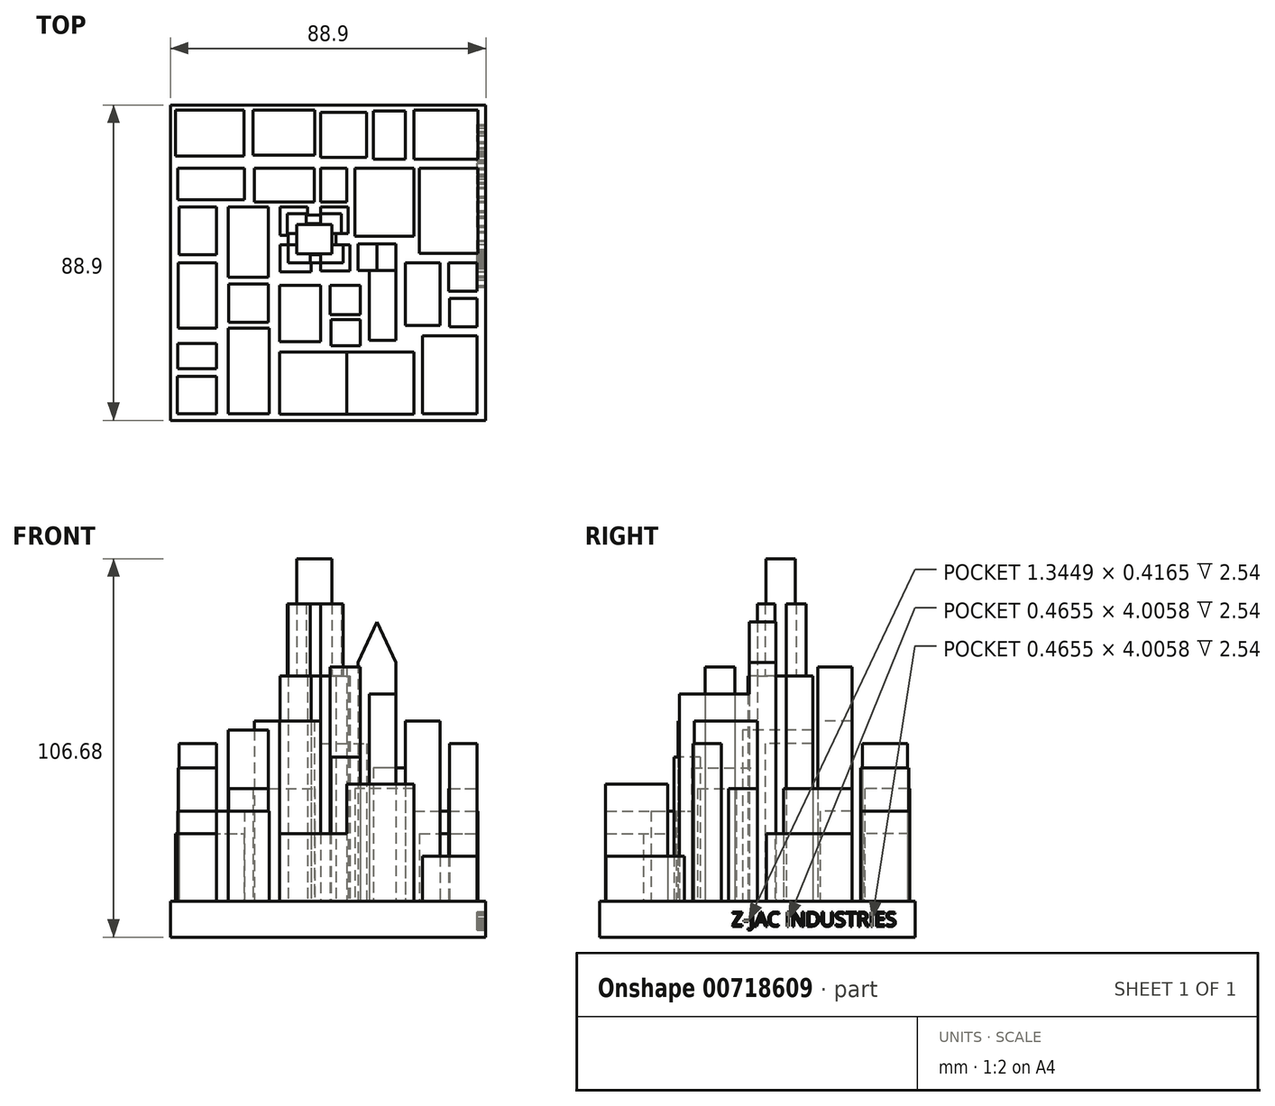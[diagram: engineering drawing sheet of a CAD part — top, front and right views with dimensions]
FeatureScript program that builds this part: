
annotation { "Feature Type Name" : "Feature", "Feature Type Description" : "" }
export const myFeature = defineFeature(function(context is Context, id is Id, definition is map)
    precondition{}
    {
        {
            var Q0;
            Q0=qCreatedBy(makeId("Top.planeOp"),FACE);
            var sketch = newSketch(context, id + "F0", { "sketchPlane" : qUnion([Q0])});
            skLineSegment(sketch, "E0", {"start": v(0, 0) * mm, "end": v(0, 44.45) * mm});
            skLineSegment(sketch, "E1", {"start": v(0, 44.45) * mm, "end": v(46.53, 44.45) * mm});
            skLineSegment(sketch, "E2", {"start": v(46.53, 44.45) * mm, "end": v(46.53, -44.45) * mm});
            skLineSegment(sketch, "E3", {"start": v(46.53, -44.45) * mm, "end": v(-42.37, -44.45) * mm});
            skLineSegment(sketch, "E4", {"start": v(-42.37, -44.45) * mm, "end": v(-42.37, 44.45) * mm});
            skLineSegment(sketch, "E5", {"start": v(-42.37, 44.45) * mm, "end": v(0, 44.45) * mm});
            skSolve(sketch);
        }
        {
            var Q0;
            Q0 = qSketchRegion(id + "F0", true);
            var Q1;
            Q1=makeQuery(id+"F0.imprint","IMPRINT",FACE,{"disambiguationData":[TD([[makeQuery(id+"F0.imprint","IMPRINT",EDGE,{"derivedFrom":sQuery(id+"F0.wireOp",EDGE,"E1")}),-1.0]])]});
            extrude(context, id + "F1", {"entities" : qUnion([Q0, Q1]), "depth" : 10.16 * mm, "offsetDistance" : 25.4 * mm});
        }
        {
            var Q0;
            Q0=makeQuery(id+"F1.opExtrude","CAP_FACE",FACE,{"disambiguationData":[OSD([sQuery(id+"F0.wireOp",EDGE,"E1"),sQuery(id+"F0.wireOp",EDGE,"E2"),sQuery(id+"F0.wireOp",EDGE,"E3"),sQuery(id+"F0.wireOp",EDGE,"E4"),sQuery(id+"F0.wireOp",EDGE,"E5")])],"isStart":false});
            var sketch = newSketch(context, id + "F2", { "sketchPlane" : qUnion([Q0])});
            skLineSegment(sketch, "E6.bottom", {"start": v(-40.9, 43.05) * mm, "end": v(-21.56, 43.05) * mm});
            skLineSegment(sketch, "E6.top", {"start": v(-40.9, 29.98) * mm, "end": v(-21.56, 29.98) * mm});
            skLineSegment(sketch, "E6.left", {"start": v(-40.9, 43.05) * mm, "end": v(-40.9, 29.98) * mm});
            skLineSegment(sketch, "E6.right", {"start": v(-21.56, 43.05) * mm, "end": v(-21.56, 29.98) * mm});
            skLineSegment(sketch, "E7.bottom", {"start": v(-11.52, -42.72) * mm, "end": v(26.25, -42.72) * mm});
            skLineSegment(sketch, "E7.top", {"start": v(-11.52, -25.17) * mm, "end": v(26.25, -25.17) * mm});
            skLineSegment(sketch, "E7.left", {"start": v(-11.52, -42.72) * mm, "end": v(-11.52, -25.17) * mm});
            skLineSegment(sketch, "E7.right", {"start": v(26.25, -42.72) * mm, "end": v(26.25, -25.17) * mm});
            skLineSegment(sketch, "E8.bottom", {"start": v(27.79, 26.67) * mm, "end": v(44.29, 26.67) * mm});
            skLineSegment(sketch, "E8.top", {"start": v(27.79, 2.59) * mm, "end": v(44.29, 2.59) * mm});
            skLineSegment(sketch, "E8.left", {"start": v(27.79, 26.67) * mm, "end": v(27.79, 2.59) * mm});
            skLineSegment(sketch, "E8.right", {"start": v(44.29, 26.67) * mm, "end": v(44.29, 2.59) * mm});
            skLineSegment(sketch, "E9.bottom", {"start": v(-40.37, -42.59) * mm, "end": v(-29.36, -42.59) * mm});
            skLineSegment(sketch, "E9.top", {"start": v(-40.37, -32.12) * mm, "end": v(-29.36, -32.12) * mm});
            skLineSegment(sketch, "E9.left", {"start": v(-40.37, -42.59) * mm, "end": v(-40.37, -32.12) * mm});
            skLineSegment(sketch, "E9.right", {"start": v(-29.36, -42.59) * mm, "end": v(-29.36, -32.12) * mm});
            skSolve(sketch);
        }
        {
            var Q0;
            Q0 = qSketchRegion(id + "F2", true);
            extrude(context, id + "F3", {"entities" : qUnion([Q0]), "operationType" : NewBodyOperationType.ADD, "depth" : 19.05 * mm, "offsetDistance" : 25.4 * mm});
        }
        {
            var Q0;
            Q0=makeQuery(id+"F1.opExtrude","CAP_FACE",FACE,{"disambiguationData":[OSD([sQuery(id+"F0.wireOp",EDGE,"E1"),sQuery(id+"F0.wireOp",EDGE,"E2"),sQuery(id+"F0.wireOp",EDGE,"E3"),sQuery(id+"F0.wireOp",EDGE,"E4"),sQuery(id+"F0.wireOp",EDGE,"E5")])],"isStart":false});
            var sketch = newSketch(context, id + "F4", { "sketchPlane" : qUnion([Q0])});
            skLineSegment(sketch, "E10.bottom", {"start": v(-26.07, -42.59) * mm, "end": v(-14.5, -42.59) * mm});
            skLineSegment(sketch, "E10.top", {"start": v(-26.07, -18.49) * mm, "end": v(-14.5, -18.49) * mm});
            skLineSegment(sketch, "E10.left", {"start": v(-26.07, -42.59) * mm, "end": v(-26.07, -18.49) * mm});
            skLineSegment(sketch, "E10.right", {"start": v(-14.5, -42.59) * mm, "end": v(-14.5, -18.49) * mm});
            skLineSegment(sketch, "E11.bottom", {"start": v(-29.36, -29.86) * mm, "end": v(-40.29, -29.86) * mm});
            skLineSegment(sketch, "E11.top", {"start": v(-29.36, -22.85) * mm, "end": v(-40.29, -22.85) * mm});
            skLineSegment(sketch, "E11.left", {"start": v(-29.36, -29.86) * mm, "end": v(-29.36, -22.85) * mm});
            skLineSegment(sketch, "E11.right", {"start": v(-40.29, -29.86) * mm, "end": v(-40.29, -22.85) * mm});
            skLineSegment(sketch, "E12.bottom", {"start": v(26.26, 42.94) * mm, "end": v(44.27, 42.94) * mm});
            skLineSegment(sketch, "E12.top", {"start": v(26.26, 29.1) * mm, "end": v(44.27, 29.1) * mm});
            skLineSegment(sketch, "E12.left", {"start": v(26.26, 42.94) * mm, "end": v(26.26, 29.1) * mm});
            skLineSegment(sketch, "E12.right", {"start": v(44.27, 42.94) * mm, "end": v(44.27, 29.1) * mm});
            skLineSegment(sketch, "E13.bottom", {"start": v(-40.29, 26.67) * mm, "end": v(-21.52, 26.67) * mm});
            skLineSegment(sketch, "E13.top", {"start": v(-40.29, 17.73) * mm, "end": v(-21.52, 17.73) * mm});
            skLineSegment(sketch, "E13.left", {"start": v(-40.29, 26.67) * mm, "end": v(-40.29, 17.73) * mm});
            skLineSegment(sketch, "E13.right", {"start": v(-21.52, 26.67) * mm, "end": v(-21.52, 17.73) * mm});
            skSolve(sketch);
        }
        {
            var Q0;
            Q0 = qSketchRegion(id + "F4", true);
            extrude(context, id + "F5", {"entities" : qUnion([Q0]), "operationType" : NewBodyOperationType.ADD, "depth" : 25.4 * mm, "offsetDistance" : 25.4 * mm});
        }
        {
            var Q0;
            Q0=makeQuery(id+"F1.opExtrude","CAP_FACE",FACE,{"disambiguationData":[OSD([sQuery(id+"F0.wireOp",EDGE,"E1"),sQuery(id+"F0.wireOp",EDGE,"E2"),sQuery(id+"F0.wireOp",EDGE,"E3"),sQuery(id+"F0.wireOp",EDGE,"E4"),sQuery(id+"F0.wireOp",EDGE,"E5")])],"isStart":false});
            var sketch = newSketch(context, id + "F6", { "sketchPlane" : qUnion([Q0])});
            skLineSegment(sketch, "E14.bottom", {"start": v(-14.7, -16.78) * mm, "end": v(-25.88, -16.78) * mm});
            skLineSegment(sketch, "E14.top", {"start": v(-14.7, -5.97) * mm, "end": v(-25.88, -5.97) * mm});
            skLineSegment(sketch, "E14.left", {"start": v(-14.7, -16.78) * mm, "end": v(-14.7, -5.97) * mm});
            skLineSegment(sketch, "E14.right", {"start": v(-25.88, -16.78) * mm, "end": v(-25.88, -5.97) * mm});
            skLineSegment(sketch, "E15.bottom", {"start": v(-19.05, 42.94) * mm, "end": v(-1.61, 42.94) * mm});
            skLineSegment(sketch, "E15.top", {"start": v(-19.05, 30.24) * mm, "end": v(-1.61, 30.24) * mm});
            skLineSegment(sketch, "E15.left", {"start": v(-19.05, 42.94) * mm, "end": v(-19.05, 30.24) * mm});
            skLineSegment(sketch, "E15.right", {"start": v(-1.61, 42.94) * mm, "end": v(-1.61, 30.24) * mm});
            skPoint(sketch, "E16.firstSnap0", {"position": v(36.04, 2.59) * mm});
            skLineSegment(sketch, "E16.bottom", {"start": v(36.04, 0) * mm, "end": v(44.08, 0) * mm});
            skLineSegment(sketch, "E16.top", {"start": v(36.04, -8.06) * mm, "end": v(44.08, -8.06) * mm});
            skLineSegment(sketch, "E16.left", {"start": v(36.04, 0) * mm, "end": v(36.04, -8.06) * mm});
            skLineSegment(sketch, "E16.right", {"start": v(44.08, 0) * mm, "end": v(44.08, -8.06) * mm});
            skPoint(sketch, "E17.firstSnap0", {"position": v(-30.9, 26.67) * mm});
            skPoint(sketch, "E17.firstSnap1", {"position": v(26.25, -33.95) * mm});
            skLineSegment(sketch, "E17.bottom", {"start": v(26.25, 26.67) * mm, "end": v(9.57, 26.67) * mm});
            skLineSegment(sketch, "E17.top", {"start": v(26.25, 7.49) * mm, "end": v(9.57, 7.49) * mm});
            skLineSegment(sketch, "E17.left", {"start": v(26.25, 26.67) * mm, "end": v(26.25, 7.49) * mm});
            skLineSegment(sketch, "E17.right", {"start": v(9.57, 26.67) * mm, "end": v(9.57, 7.49) * mm});
            skSolve(sketch);
        }
        {
            var Q0;
            Q0 = qSketchRegion(id + "F6", true);
            extrude(context, id + "F7", {"entities" : qUnion([Q0]), "operationType" : NewBodyOperationType.ADD, "depth" : 31.75 * mm, "offsetDistance" : 25.4 * mm});
        }
        {
            var Q0;
            Q0=makeQuery(id+"F1.opExtrude","CAP_FACE",FACE,{"disambiguationData":[OSD([sQuery(id+"F0.wireOp",EDGE,"E1"),sQuery(id+"F0.wireOp",EDGE,"E2"),sQuery(id+"F0.wireOp",EDGE,"E3"),sQuery(id+"F0.wireOp",EDGE,"E4"),sQuery(id+"F0.wireOp",EDGE,"E5")])],"isStart":false});
            var sketch = newSketch(context, id + "F8", { "sketchPlane" : qUnion([Q0])});
            skLineSegment(sketch, "E18.bottom", {"start": v(23.8, 29.1) * mm, "end": v(14.88, 29.1) * mm});
            skLineSegment(sketch, "E18.top", {"start": v(23.8, 42.75) * mm, "end": v(14.88, 42.75) * mm});
            skLineSegment(sketch, "E18.left", {"start": v(23.8, 29.1) * mm, "end": v(23.8, 42.75) * mm});
            skLineSegment(sketch, "E18.right", {"start": v(14.88, 29.1) * mm, "end": v(14.88, 42.75) * mm});
            skLineSegment(sketch, "E19.bottom", {"start": v(-29.36, -18.49) * mm, "end": v(-40.1, -18.49) * mm});
            skLineSegment(sketch, "E19.top", {"start": v(-29.36, 0) * mm, "end": v(-40.1, 0) * mm});
            skLineSegment(sketch, "E19.left", {"start": v(-29.36, -18.49) * mm, "end": v(-29.36, 0) * mm});
            skLineSegment(sketch, "E19.right", {"start": v(-40.1, -18.49) * mm, "end": v(-40.1, 0) * mm});
            skSolve(sketch);
        }
        {
            var Q0;
            Q0 = qSketchRegion(id + "F8", true);
            extrude(context, id + "F9", {"entities" : qUnion([Q0]), "operationType" : NewBodyOperationType.ADD, "depth" : 37.6 * mm, "offsetDistance" : 25.4 * mm});
        }
        {
            var Q0;
            Q0=makeQuery(id+"F1.opExtrude","CAP_FACE",FACE,{"disambiguationData":[OSD([sQuery(id+"F0.wireOp",EDGE,"E1"),sQuery(id+"F0.wireOp",EDGE,"E2"),sQuery(id+"F0.wireOp",EDGE,"E3"),sQuery(id+"F0.wireOp",EDGE,"E4"),sQuery(id+"F0.wireOp",EDGE,"E5")])],"isStart":false});
            var sketch = newSketch(context, id + "F10", { "sketchPlane" : qUnion([Q0])});
            skLineSegment(sketch, "E20.bottom", {"start": v(-39.91, 15.64) * mm, "end": v(-29.36, 15.64) * mm});
            skLineSegment(sketch, "E20.top", {"start": v(-39.91, 2.18) * mm, "end": v(-29.36, 2.18) * mm});
            skLineSegment(sketch, "E20.left", {"start": v(-39.91, 15.64) * mm, "end": v(-39.91, 2.18) * mm});
            skLineSegment(sketch, "E20.right", {"start": v(-29.36, 15.64) * mm, "end": v(-29.36, 2.18) * mm});
            skLineSegment(sketch, "E21.bottom", {"start": v(36.3, -10.14) * mm, "end": v(44.08, -10.14) * mm});
            skLineSegment(sketch, "E21.top", {"start": v(36.3, -18.1) * mm, "end": v(44.08, -18.1) * mm});
            skLineSegment(sketch, "E21.left", {"start": v(36.3, -10.14) * mm, "end": v(36.3, -18.1) * mm});
            skLineSegment(sketch, "E21.right", {"start": v(44.08, -10.14) * mm, "end": v(44.08, -18.1) * mm});
            skLineSegment(sketch, "E22.bottom", {"start": v(0, 42.37) * mm, "end": v(12.99, 42.37) * mm});
            skLineSegment(sketch, "E22.top", {"start": v(0, 29.67) * mm, "end": v(12.99, 29.67) * mm});
            skLineSegment(sketch, "E22.left", {"start": v(0, 42.37) * mm, "end": v(0, 29.67) * mm});
            skLineSegment(sketch, "E22.right", {"start": v(12.99, 42.37) * mm, "end": v(12.99, 29.67) * mm});
            skSolve(sketch);
        }
        {
            var Q0;
            Q0 = qSketchRegion(id + "F10", true);
            extrude(context, id + "F11", {"entities" : qUnion([Q0]), "operationType" : NewBodyOperationType.ADD, "depth" : 44.45 * mm, "offsetDistance" : 25.4 * mm});
        }
        {
            var Q0;
            Q0=makeQuery(id+"F1.opExtrude","CAP_FACE",FACE,{"disambiguationData":[OSD([sQuery(id+"F0.wireOp",EDGE,"E1"),sQuery(id+"F0.wireOp",EDGE,"E2"),sQuery(id+"F0.wireOp",EDGE,"E3"),sQuery(id+"F0.wireOp",EDGE,"E4"),sQuery(id+"F0.wireOp",EDGE,"E5")])],"isStart":false});
            var sketch = newSketch(context, id + "F12", { "sketchPlane" : qUnion([Q0])});
            skLineSegment(sketch, "E23.bottom", {"start": v(-26.07, 15.64) * mm, "end": v(-14.7, 15.64) * mm});
            skLineSegment(sketch, "E23.top", {"start": v(-26.07, -4.08) * mm, "end": v(-14.7, -4.08) * mm});
            skLineSegment(sketch, "E23.left", {"start": v(-26.07, 15.64) * mm, "end": v(-26.07, -4.08) * mm});
            skLineSegment(sketch, "E23.right", {"start": v(-14.7, 15.64) * mm, "end": v(-14.7, -4.08) * mm});
            skSolve(sketch);
        }
        {
            var Q0;
            Q0 = qSketchRegion(id + "F12", true);
            extrude(context, id + "F13", {"entities" : qUnion([Q0]), "operationType" : NewBodyOperationType.ADD, "depth" : 48.26 * mm, "offsetDistance" : 25.4 * mm});
        }
        {
            var Q0;
            Q0=makeQuery(id+"F1.opExtrude","CAP_FACE",FACE,{"disambiguationData":[OSD([sQuery(id+"F0.wireOp",EDGE,"E1"),sQuery(id+"F0.wireOp",EDGE,"E2"),sQuery(id+"F0.wireOp",EDGE,"E3"),sQuery(id+"F0.wireOp",EDGE,"E4"),sQuery(id+"F0.wireOp",EDGE,"E5")])],"isStart":false});
            var sketch = newSketch(context, id + "F14", { "sketchPlane" : qUnion([Q0])});
            skLineSegment(sketch, "E24.bottom", {"start": v(44.08, -20.57) * mm, "end": v(28.72, -20.57) * mm});
            skLineSegment(sketch, "E24.top", {"start": v(44.08, -42.56) * mm, "end": v(28.72, -42.56) * mm});
            skLineSegment(sketch, "E24.left", {"start": v(44.08, -20.57) * mm, "end": v(44.08, -42.56) * mm});
            skLineSegment(sketch, "E24.right", {"start": v(28.72, -20.57) * mm, "end": v(28.72, -42.56) * mm});
            skSolve(sketch);
        }
        {
            var Q0;
            Q0 = qSketchRegion(id + "F14", true);
            extrude(context, id + "F15", {"entities" : qUnion([Q0]), "operationType" : NewBodyOperationType.ADD, "depth" : 12.7 * mm, "offsetDistance" : 25.4 * mm});
        }
        {
            var Q0;
            Q0=makeQuery(id+"F1.opExtrude","CAP_FACE",FACE,{"disambiguationData":[OSD([sQuery(id+"F0.wireOp",EDGE,"E1"),sQuery(id+"F0.wireOp",EDGE,"E2"),sQuery(id+"F0.wireOp",EDGE,"E3"),sQuery(id+"F0.wireOp",EDGE,"E4"),sQuery(id+"F0.wireOp",EDGE,"E5")])],"isStart":false});
            var sketch = newSketch(context, id + "F16", { "sketchPlane" : qUnion([Q0])});
            skPoint(sketch, "E25.oppositeSnap0", {"position": v(9.57, 17.08) * mm});
            skLineSegment(sketch, "E25.bottom", {"start": v(-18.68, 26.67) * mm, "end": v(-1.8, 26.67) * mm});
            skLineSegment(sketch, "E25.top", {"start": v(-18.68, 17.08) * mm, "end": v(-1.8, 17.08) * mm});
            skLineSegment(sketch, "E25.left", {"start": v(-18.68, 26.67) * mm, "end": v(-18.68, 17.08) * mm});
            skLineSegment(sketch, "E25.right", {"start": v(-1.8, 26.67) * mm, "end": v(-1.8, 17.08) * mm});
            skLineSegment(sketch, "E26.bottom", {"start": v(33.65, 0) * mm, "end": v(23.8, 0) * mm});
            skLineSegment(sketch, "E26.top", {"start": v(33.65, -17.73) * mm, "end": v(23.8, -17.73) * mm});
            skLineSegment(sketch, "E26.left", {"start": v(33.65, 0) * mm, "end": v(33.65, -17.73) * mm});
            skLineSegment(sketch, "E26.right", {"start": v(23.8, 0) * mm, "end": v(23.8, -17.73) * mm});
            skLineSegment(sketch, "E27.bottom", {"start": v(-11.52, -22.28) * mm, "end": v(0, -22.28) * mm});
            skLineSegment(sketch, "E27.top", {"start": v(-11.52, -6.35) * mm, "end": v(0, -6.35) * mm});
            skLineSegment(sketch, "E27.left", {"start": v(-11.52, -22.28) * mm, "end": v(-11.52, -6.35) * mm});
            skLineSegment(sketch, "E27.right", {"start": v(0, -22.28) * mm, "end": v(0, -6.35) * mm});
            skSolve(sketch);
        }
        {
            var Q0;
            Q0 = qSketchRegion(id + "F16", true);
            extrude(context, id + "F17", {"entities" : qUnion([Q0]), "operationType" : NewBodyOperationType.ADD, "depth" : 50.8 * mm, "offsetDistance" : 25.4 * mm});
        }
        {
            var Q0;
            Q0=makeQuery(id+"F1.opExtrude","CAP_FACE",FACE,{"disambiguationData":[OSD([sQuery(id+"F0.wireOp",EDGE,"E1"),sQuery(id+"F0.wireOp",EDGE,"E2"),sQuery(id+"F0.wireOp",EDGE,"E3"),sQuery(id+"F0.wireOp",EDGE,"E4"),sQuery(id+"F0.wireOp",EDGE,"E5")])],"isStart":false});
            var sketch = newSketch(context, id + "F18", { "sketchPlane" : qUnion([Q0])});
            skLineSegment(sketch, "E28.bottom", {"start": v(-9.2, 13.46) * mm, "end": v(4.27, 13.46) * mm});
            skLineSegment(sketch, "E28.top", {"start": v(-9.2, 0) * mm, "end": v(4.27, 0) * mm});
            skLineSegment(sketch, "E28.left", {"start": v(-9.2, 13.46) * mm, "end": v(-9.2, 0) * mm});
            skLineSegment(sketch, "E28.right", {"start": v(4.27, 13.46) * mm, "end": v(4.27, 0) * mm});
            skLineSegment(sketch, "E29.bottom", {"start": v(-11.47, 15.64) * mm, "end": v(-3.7, 15.64) * mm});
            skLineSegment(sketch, "E29.top", {"start": v(-11.47, 7.68) * mm, "end": v(-3.7, 7.68) * mm});
            skLineSegment(sketch, "E29.left", {"start": v(-11.47, 15.64) * mm, "end": v(-11.47, 7.68) * mm});
            skLineSegment(sketch, "E29.right", {"start": v(-3.7, 15.64) * mm, "end": v(-3.7, 7.68) * mm});
            skLineSegment(sketch, "E30.bottom", {"start": v(0, 15.64) * mm, "end": v(7.68, 15.64) * mm});
            skLineSegment(sketch, "E30.top", {"start": v(0, 8.25) * mm, "end": v(7.68, 8.25) * mm});
            skLineSegment(sketch, "E30.left", {"start": v(0, 15.64) * mm, "end": v(0, 8.25) * mm});
            skLineSegment(sketch, "E30.right", {"start": v(7.68, 15.64) * mm, "end": v(7.68, 8.25) * mm});
            skLineSegment(sketch, "E31.bottom", {"start": v(0, 5.02) * mm, "end": v(8.25, 5.02) * mm});
            skLineSegment(sketch, "E31.top", {"start": v(0, -2.37) * mm, "end": v(8.25, -2.37) * mm});
            skLineSegment(sketch, "E31.left", {"start": v(0, 5.02) * mm, "end": v(0, -2.37) * mm});
            skLineSegment(sketch, "E31.right", {"start": v(8.25, 5.02) * mm, "end": v(8.25, -2.37) * mm});
            skLineSegment(sketch, "E32.bottom", {"start": v(-2.75, 5.02) * mm, "end": v(-11.47, 5.02) * mm});
            skLineSegment(sketch, "E32.top", {"start": v(-2.75, -2.56) * mm, "end": v(-11.47, -2.56) * mm});
            skLineSegment(sketch, "E32.left", {"start": v(-2.75, 5.02) * mm, "end": v(-2.75, -2.56) * mm});
            skLineSegment(sketch, "E32.right", {"start": v(-11.47, 5.02) * mm, "end": v(-11.47, -2.56) * mm});
            skSolve(sketch);
        }
        {
            var Q0;
            Q0 = qSketchRegion(id + "F18", true);
            extrude(context, id + "F19", {"entities" : qUnion([Q0]), "operationType" : NewBodyOperationType.ADD, "depth" : 63.5 * mm, "offsetDistance" : 25.4 * mm});
        }
        {
            var Q0;
            Q0=makeQuery(id+"F19.opExtrude","CAP_FACE",FACE,{"disambiguationData":[OSD([sQuery(id+"F18.wireOp",EDGE,"E28.bottom"),sQuery(id+"F18.wireOp",EDGE,"E28.top"),sQuery(id+"F18.wireOp",EDGE,"E28.left"),sQuery(id+"F18.wireOp",EDGE,"E28.right"),sQuery(id+"F18.wireOp",EDGE,"E29.bottom"),sQuery(id+"F18.wireOp",EDGE,"E29.top"),sQuery(id+"F18.wireOp",EDGE,"E29.left"),sQuery(id+"F18.wireOp",EDGE,"E29.right"),sQuery(id+"F18.wireOp",EDGE,"E30.bottom"),sQuery(id+"F18.wireOp",EDGE,"E30.top"),sQuery(id+"F18.wireOp",EDGE,"E30.left"),sQuery(id+"F18.wireOp",EDGE,"E30.right"),sQuery(id+"F18.wireOp",EDGE,"E31.bottom"),sQuery(id+"F18.wireOp",EDGE,"E31.top"),sQuery(id+"F18.wireOp",EDGE,"E31.left"),sQuery(id+"F18.wireOp",EDGE,"E31.right"),sQuery(id+"F18.wireOp",EDGE,"E32.bottom"),sQuery(id+"F18.wireOp",EDGE,"E32.top"),sQuery(id+"F18.wireOp",EDGE,"E32.left"),sQuery(id+"F18.wireOp",EDGE,"E32.right")])],"isStart":false});
            var sketch = newSketch(context, id + "F20", { "sketchPlane" : qUnion([Q0])});
            skLineSegment(sketch, "E33.bottom", {"start": v(-9.39, 13.75) * mm, "end": v(-4.08, 13.75) * mm});
            skLineSegment(sketch, "E33.top", {"start": v(-9.39, 8.25) * mm, "end": v(-4.08, 8.25) * mm});
            skLineSegment(sketch, "E33.left", {"start": v(-9.39, 13.75) * mm, "end": v(-9.39, 8.25) * mm});
            skLineSegment(sketch, "E33.right", {"start": v(-4.08, 13.75) * mm, "end": v(-4.08, 8.25) * mm});
            skLineSegment(sketch, "E34.bottom", {"start": v(-9.2, 0) * mm, "end": v(-2.94, 0) * mm});
            skLineSegment(sketch, "E34.top", {"start": v(-9.2, 5.02) * mm, "end": v(-2.94, 5.02) * mm});
            skLineSegment(sketch, "E34.left", {"start": v(-9.2, 0) * mm, "end": v(-9.2, 5.02) * mm});
            skLineSegment(sketch, "E34.right", {"start": v(-2.94, 0) * mm, "end": v(-2.94, 5.02) * mm});
            skLineSegment(sketch, "E35.bottom", {"start": v(6.35, 0) * mm, "end": v(0, 0) * mm});
            skLineSegment(sketch, "E35.top", {"start": v(6.35, 5.02) * mm, "end": v(0, 5.02) * mm});
            skLineSegment(sketch, "E35.left", {"start": v(6.35, 0) * mm, "end": v(6.35, 5.02) * mm});
            skLineSegment(sketch, "E35.right", {"start": v(0, 0) * mm, "end": v(0, 5.02) * mm});
            skLineSegment(sketch, "E36.bottom", {"start": v(5.78, 13.75) * mm, "end": v(0, 13.75) * mm});
            skLineSegment(sketch, "E36.top", {"start": v(5.78, 8.25) * mm, "end": v(0, 8.25) * mm});
            skLineSegment(sketch, "E36.left", {"start": v(5.78, 13.75) * mm, "end": v(5.78, 8.25) * mm});
            skLineSegment(sketch, "E36.right", {"start": v(0, 13.75) * mm, "end": v(0, 8.25) * mm});
            skPoint(sketch, "E37.firstSnap0", {"position": v(-6.73, 13.75) * mm});
            skPoint(sketch, "E37.firstSnap1", {"position": v(-4.08, 11) * mm});
            skPoint(sketch, "E37.oppositeSnap0", {"position": v(3.18, 5.02) * mm});
            skLineSegment(sketch, "E37.bottom", {"start": v(-6.73, 11) * mm, "end": v(3.18, 11) * mm});
            skLineSegment(sketch, "E37.top", {"start": v(-6.73, 2.18) * mm, "end": v(3.18, 2.18) * mm});
            skLineSegment(sketch, "E37.left", {"start": v(-6.73, 11) * mm, "end": v(-6.73, 2.18) * mm});
            skLineSegment(sketch, "E37.right", {"start": v(3.18, 11) * mm, "end": v(3.18, 2.18) * mm});
            skSolve(sketch);
        }
        {
            var Q0;
            Q0 = qSketchRegion(id + "F20", true);
            extrude(context, id + "F21", {"entities" : qUnion([Q0]), "operationType" : NewBodyOperationType.ADD, "depth" : 20.32 * mm, "offsetDistance" : 25.4 * mm});
        }
        {
            var Q0;
            Q0=makeQuery(id+"F21.opExtrude","CAP_FACE",FACE,{"disambiguationData":[OSD([sQuery(id+"F20.wireOp",EDGE,"E33.bottom"),sQuery(id+"F20.wireOp",EDGE,"E33.top"),sQuery(id+"F20.wireOp",EDGE,"E33.left"),sQuery(id+"F20.wireOp",EDGE,"E33.right"),sQuery(id+"F20.wireOp",EDGE,"E34.bottom"),sQuery(id+"F20.wireOp",EDGE,"E34.top"),sQuery(id+"F20.wireOp",EDGE,"E34.left"),sQuery(id+"F20.wireOp",EDGE,"E34.right"),sQuery(id+"F20.wireOp",EDGE,"E35.bottom"),sQuery(id+"F20.wireOp",EDGE,"E35.top"),sQuery(id+"F20.wireOp",EDGE,"E35.left"),sQuery(id+"F20.wireOp",EDGE,"E35.right"),sQuery(id+"F20.wireOp",EDGE,"E36.bottom"),sQuery(id+"F20.wireOp",EDGE,"E36.top"),sQuery(id+"F20.wireOp",EDGE,"E36.left"),sQuery(id+"F20.wireOp",EDGE,"E36.right"),sQuery(id+"F20.wireOp",EDGE,"E37.bottom"),sQuery(id+"F20.wireOp",EDGE,"E37.top"),sQuery(id+"F20.wireOp",EDGE,"E37.left"),sQuery(id+"F20.wireOp",EDGE,"E37.right")])],"isStart":false});
            var sketch = newSketch(context, id + "F22", { "sketchPlane" : qUnion([Q0])});
            skPoint(sketch, "E38.oppositeSnap0", {"position": v(6.35, 2.51) * mm});
            skLineSegment(sketch, "E38.bottom", {"start": v(-6.73, 10.71) * mm, "end": v(3.18, 10.71) * mm});
            skLineSegment(sketch, "E38.top", {"start": v(-6.73, 2.51) * mm, "end": v(3.18, 2.51) * mm});
            skLineSegment(sketch, "E38.left", {"start": v(-6.73, 10.71) * mm, "end": v(-6.73, 2.51) * mm});
            skLineSegment(sketch, "E38.right", {"start": v(3.18, 10.71) * mm, "end": v(3.18, 2.51) * mm});
            skSolve(sketch);
        }
        {
            var Q0;
            Q0 = qSketchRegion(id + "F22", true);
            extrude(context, id + "F23", {"entities" : qUnion([Q0]), "operationType" : NewBodyOperationType.ADD, "depth" : 12.7 * mm, "offsetDistance" : 25.4 * mm});
        }
        {
            var Q0;
            Q0=makeQuery(id+"F1.opExtrude","CAP_FACE",FACE,{"disambiguationData":[OSD([sQuery(id+"F0.wireOp",EDGE,"E1"),sQuery(id+"F0.wireOp",EDGE,"E2"),sQuery(id+"F0.wireOp",EDGE,"E3"),sQuery(id+"F0.wireOp",EDGE,"E4"),sQuery(id+"F0.wireOp",EDGE,"E5")])],"isStart":false});
            var sketch = newSketch(context, id + "F24", { "sketchPlane" : qUnion([Q0])});
            skPoint(sketch, "E39.oppositeSnap0", {"position": v(9.57, 17.08) * mm});
            skLineSegment(sketch, "E39.bottom", {"start": v(0, 26.67) * mm, "end": v(7.3, 26.67) * mm});
            skLineSegment(sketch, "E39.top", {"start": v(0, 17.08) * mm, "end": v(7.3, 17.08) * mm});
            skLineSegment(sketch, "E39.left", {"start": v(0, 26.67) * mm, "end": v(0, 17.08) * mm});
            skLineSegment(sketch, "E39.right", {"start": v(7.3, 26.67) * mm, "end": v(7.3, 17.08) * mm});
            skLineSegment(sketch, "E40.bottom", {"start": v(2.61, -6.35) * mm, "end": v(11.2, -6.35) * mm});
            skLineSegment(sketch, "E40.top", {"start": v(2.61, -14.66) * mm, "end": v(11.2, -14.66) * mm});
            skLineSegment(sketch, "E40.left", {"start": v(2.61, -6.35) * mm, "end": v(2.61, -14.66) * mm});
            skLineSegment(sketch, "E40.right", {"start": v(11.2, -6.35) * mm, "end": v(11.2, -14.66) * mm});
            skSolve(sketch);
        }
        {
            var Q0;
            Q0 = qSketchRegion(id + "F24", true);
            extrude(context, id + "F25", {"entities" : qUnion([Q0]), "operationType" : NewBodyOperationType.ADD, "depth" : 66.04 * mm, "offsetDistance" : 25.4 * mm});
        }
        {
            var Q0;
            Q0=makeQuery(id+"F1.opExtrude","CAP_FACE",FACE,{"disambiguationData":[OSD([sQuery(id+"F0.wireOp",EDGE,"E1"),sQuery(id+"F0.wireOp",EDGE,"E2"),sQuery(id+"F0.wireOp",EDGE,"E3"),sQuery(id+"F0.wireOp",EDGE,"E4"),sQuery(id+"F0.wireOp",EDGE,"E5")])],"isStart":false});
            var sketch = newSketch(context, id + "F26", { "sketchPlane" : qUnion([Q0])});
            skLineSegment(sketch, "E41.bottom", {"start": v(10.52, 5.21) * mm, "end": v(21.14, 5.21) * mm});
            skLineSegment(sketch, "E41.top", {"start": v(10.52, -2.18) * mm, "end": v(21.14, -2.18) * mm});
            skLineSegment(sketch, "E41.left", {"start": v(10.52, 5.21) * mm, "end": v(10.52, -2.18) * mm});
            skLineSegment(sketch, "E41.right", {"start": v(21.14, 5.21) * mm, "end": v(21.14, -2.18) * mm});
            skLineSegment(sketch, "E42.bottom", {"start": v(21.14, -21.9) * mm, "end": v(13.75, -21.9) * mm});
            skLineSegment(sketch, "E42.top", {"start": v(21.14, -2.18) * mm, "end": v(13.75, -2.18) * mm});
            skLineSegment(sketch, "E42.left", {"start": v(21.14, -21.9) * mm, "end": v(21.14, -2.18) * mm});
            skLineSegment(sketch, "E42.right", {"start": v(13.75, -21.9) * mm, "end": v(13.75, -2.18) * mm});
            skSolve(sketch);
        }
        {
            var Q0;
            Q0 = qSketchRegion(id + "F26", true);
            extrude(context, id + "F27", {"entities" : qUnion([Q0]), "operationType" : NewBodyOperationType.ADD, "depth" : 58.42 * mm, "offsetDistance" : 25.4 * mm});
        }
        {
            var Q0;
            Q0=makeQuery(id+"F27.opExtrude","CAP_FACE",FACE,{"disambiguationData":[OSD([sQuery(id+"F26.wireOp",EDGE,"E41.bottom"),sQuery(id+"F26.wireOp",EDGE,"E41.top"),sQuery(id+"F26.wireOp",EDGE,"E41.left"),sQuery(id+"F26.wireOp",EDGE,"E41.right"),sQuery(id+"F26.wireOp",EDGE,"E42.bottom"),sQuery(id+"F26.wireOp",EDGE,"E42.left"),sQuery(id+"F26.wireOp",EDGE,"E42.right")])],"isStart":false});
            var sketch = newSketch(context, id + "F28", { "sketchPlane" : qUnion([Q0])});
            skLineSegment(sketch, "E43.bottom", {"start": v(10.52, 5.21) * mm, "end": v(21.14, 5.21) * mm});
            skLineSegment(sketch, "E43.top", {"start": v(10.52, -2.18) * mm, "end": v(21.14, -2.18) * mm});
            skLineSegment(sketch, "E43.left", {"start": v(10.52, 5.21) * mm, "end": v(10.52, -2.18) * mm});
            skLineSegment(sketch, "E43.right", {"start": v(21.14, 5.21) * mm, "end": v(21.14, -2.18) * mm});
            skSolve(sketch);
        }
        {
            var Q0;
            Q0 = qSketchRegion(id + "F28", true);
            extrude(context, id + "F29", {"entities" : qUnion([Q0]), "operationType" : NewBodyOperationType.ADD, "depth" : 20.32 * mm, "offsetDistance" : 25.4 * mm});
        }
        {
            var Q0;
            Q0=makeQuery(id+"F29.boolean.opBoolean","MERGE",FACE,{"derivedFrom":[makeQuery(id+"F27.opExtrude","SWEPT_FACE",FACE,{"disambiguationData":[OSD([sQuery(id+"F26.wireOp",EDGE,"E41.top")])]}),makeQuery(id+"F29.opExtrude","SWEPT_FACE",FACE,{"disambiguationData":[OSD([sQuery(id+"F28.wireOp",EDGE,"E43.top")])]})]});
            var sketch = newSketch(context, id + "F30", { "sketchPlane" : qUnion([Q0])});
            skLineSegment(sketch, "E44", {"start": v(15.83, 88.9) * mm, "end": v(10.52, 77.36) * mm});
            skLineSegment(sketch, "E45", {"start": v(10.52, 88.9) * mm, "end": v(10.52, 77.36) * mm});
            skLineSegment(sketch, "E46", {"start": v(15.83, 88.9) * mm, "end": v(10.52, 88.9) * mm});
            skLineSegment(sketch, "E47", {"start": v(15.83, 88.9) * mm, "end": v(21.14, 77.36) * mm});
            skPoint(sketch, "E47.endSnap0", {"position": v(21.14, 78.74) * mm});
            skLineSegment(sketch, "E48", {"start": v(21.14, 77.36) * mm, "end": v(21.14, 88.9) * mm});
            skLineSegment(sketch, "E49", {"start": v(21.14, 88.9) * mm, "end": v(15.83, 88.9) * mm});
            skSolve(sketch);
        }
        {
            var Q0;
            Q0 = qSketchRegion(id + "F30", true);
            extrude(context, id + "F31", {"entities" : qUnion([Q0]), "operationType" : NewBodyOperationType.REMOVE, "oppositeDirection" : true, "depth" : 25.4 * mm, "offsetDistance" : 25.4 * mm});
        }
        {
            var Q0;
            Q0=makeQuery(id+"F1.opExtrude","CAP_FACE",FACE,{"disambiguationData":[OSD([sQuery(id+"F0.wireOp",EDGE,"E1"),sQuery(id+"F0.wireOp",EDGE,"E2"),sQuery(id+"F0.wireOp",EDGE,"E3"),sQuery(id+"F0.wireOp",EDGE,"E4"),sQuery(id+"F0.wireOp",EDGE,"E5")])],"isStart":false});
            var sketch = newSketch(context, id + "F32", { "sketchPlane" : qUnion([Q0])});
            skLineSegment(sketch, "E50.bottom", {"start": v(2.94, -16.02) * mm, "end": v(11.1, -16.02) * mm});
            skLineSegment(sketch, "E50.top", {"start": v(2.94, -23.42) * mm, "end": v(11.1, -23.42) * mm});
            skLineSegment(sketch, "E50.left", {"start": v(2.94, -16.02) * mm, "end": v(2.94, -23.42) * mm});
            skLineSegment(sketch, "E50.right", {"start": v(11.1, -16.02) * mm, "end": v(11.1, -23.42) * mm});
            skSolve(sketch);
        }
        {
            var Q0;
            Q0 = qSketchRegion(id + "F32", true);
            extrude(context, id + "F33", {"entities" : qUnion([Q0]), "operationType" : NewBodyOperationType.ADD, "depth" : 40.64 * mm, "offsetDistance" : 25.4 * mm});
        }
        {
            var Q0;
            Q0=makeQuery(id+"F1.opExtrude","SWEPT_FACE",FACE,{"disambiguationData":[OSD([sQuery(id+"F0.wireOp",EDGE,"E2")])]});
            var sketch = newSketch(context, id + "F34", { "sketchPlane" : qUnion([Q0])});
            skText(sketch, "E51", { "text": "Z-JAC INDUSTRIES", "fontName": "OpenSans-Regular.ttf"});
            const initialGuessF34  = {"E51": [-0.0072, 0.00305, 1, 0, 0.00404]};
            skSetInitialGuess(sketch, initialGuessF34);
            skSolve(sketch);
        }
        {
            var Q0;
            Q0 = qSketchRegion(id + "F34", true);
            extrude(context, id + "F35", {"entities" : qUnion([Q0]), "operationType" : NewBodyOperationType.REMOVE, "oppositeDirection" : true, "depth" : 2.54 * mm, "offsetDistance" : 25.4 * mm});
        }
        {
            var Q0;
            Q0=makeQuery(id+"F3.opExtrude","CAP_FACE",FACE,{"disambiguationData":[OSD([sQuery(id+"F2.wireOp",EDGE,"E7.bottom"),sQuery(id+"F2.wireOp",EDGE,"E7.top"),sQuery(id+"F2.wireOp",EDGE,"E7.left"),sQuery(id+"F2.wireOp",EDGE,"E7.right")])],"isStart":false});
            var sketch = newSketch(context, id + "F36", { "sketchPlane" : qUnion([Q0])});
            skLineSegment(sketch, "E52.bottom", {"start": v(7.36, -25.17) * mm, "end": v(26.25, -25.17) * mm});
            skLineSegment(sketch, "E52.top", {"start": v(7.36, -42.72) * mm, "end": v(26.25, -42.72) * mm});
            skLineSegment(sketch, "E52.left", {"start": v(7.36, -25.17) * mm, "end": v(7.36, -42.72) * mm});
            skLineSegment(sketch, "E52.right", {"start": v(26.25, -25.17) * mm, "end": v(26.25, -42.72) * mm});
            skSolve(sketch);
        }
        {
            var Q0;
            Q0 = qSketchRegion(id + "F36", true);
            extrude(context, id + "F37", {"entities" : qUnion([Q0]), "operationType" : NewBodyOperationType.ADD, "depth" : 13.97 * mm, "offsetDistance" : 25.4 * mm});
        }
    });
